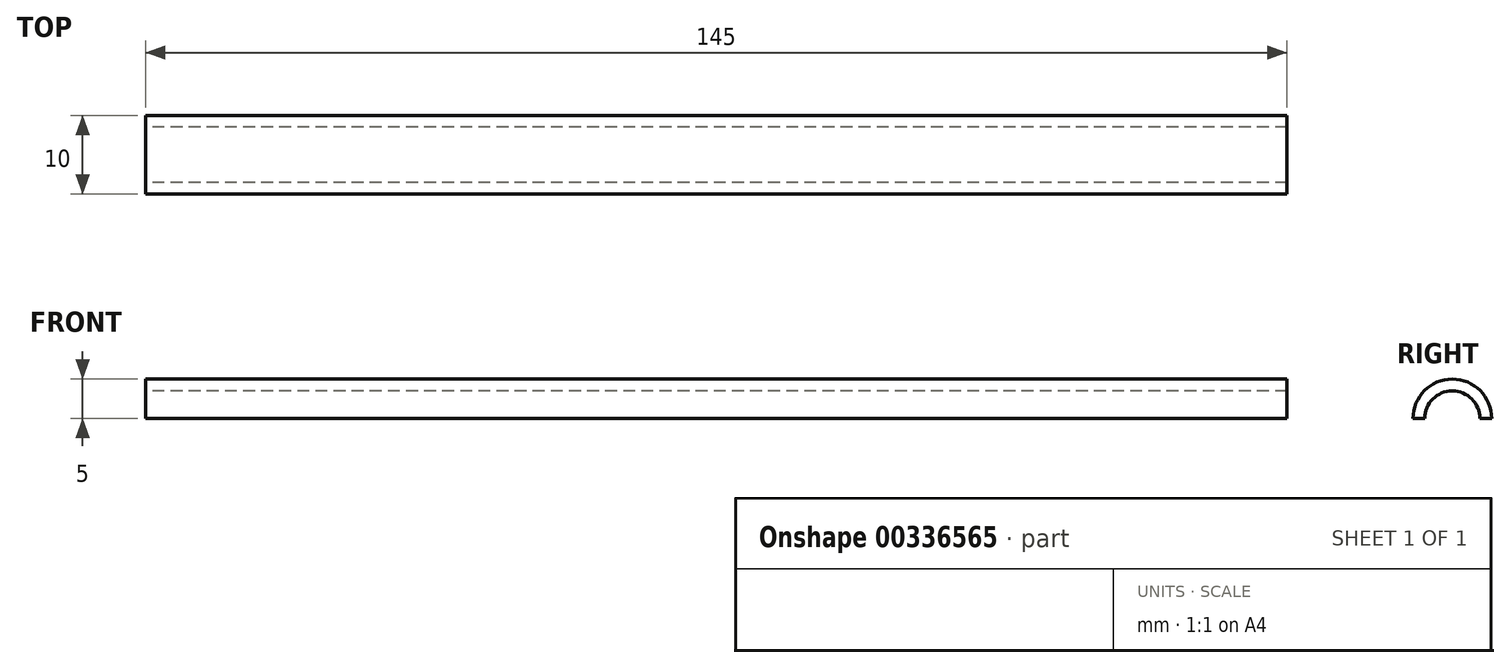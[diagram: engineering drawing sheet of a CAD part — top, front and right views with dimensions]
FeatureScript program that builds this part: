
annotation { "Feature Type Name" : "Feature", "Feature Type Description" : "" }
export const myFeature = defineFeature(function(context is Context, id is Id, definition is map)
    precondition{}
    {
        {
            var Q0;
            Q0=qCreatedBy(makeId("Right.planeOp"),FACE);
            var sketch = newSketch(context, id + "F0", { "sketchPlane" : qUnion([Q0])});
            skArc(sketch, "E0", {"start": v(5, 0) * mm, "mid": v(0, 5) * mm, "end": v(-5, 0) * mm});
            skLineSegment(sketch, "E1", {"start": v(-5, 0) * mm, "end": v(5, 0) * mm});
            skSolve(sketch);
        }
        {
            var Q0;
            Q0 = qSketchRegion(id + "F0", true);
            extrude(context, id + "F1", {"entities" : qUnion([Q0]), "oppositeDirection" : true, "depth" : 145 * mm});
        }
        {
            var Q0;
            Q0=makeQuery(id+"F1.opExtrude","CAP_FACE",FACE,{"disambiguationData":[OSD([sQuery(id+"F0.wireOp",EDGE,"E0"),sQuery(id+"F0.wireOp",EDGE,"E1")])],"isStart":false});
            var sketch = newSketch(context, id + "F2", { "sketchPlane" : qUnion([Q0])});
            skArc(sketch, "E2", {"start": v(3.5, 0) * mm, "mid": v(0, 3.5) * mm, "end": v(-3.5, 0) * mm});
            skLineSegment(sketch, "E3", {"start": v(-3.5, 0) * mm, "end": v(3.5, 0) * mm});
            skSolve(sketch);
        }
        {
            var Q0;
            Q0 = qSketchRegion(id + "F2", true);
            extrude(context, id + "F3", {"entities" : qUnion([Q0]), "operationType" : NewBodyOperationType.REMOVE, "endBound" : BoundingType.THROUGH_ALL, "oppositeDirection" : true, "depth" : 25 * mm});
        }
    });
